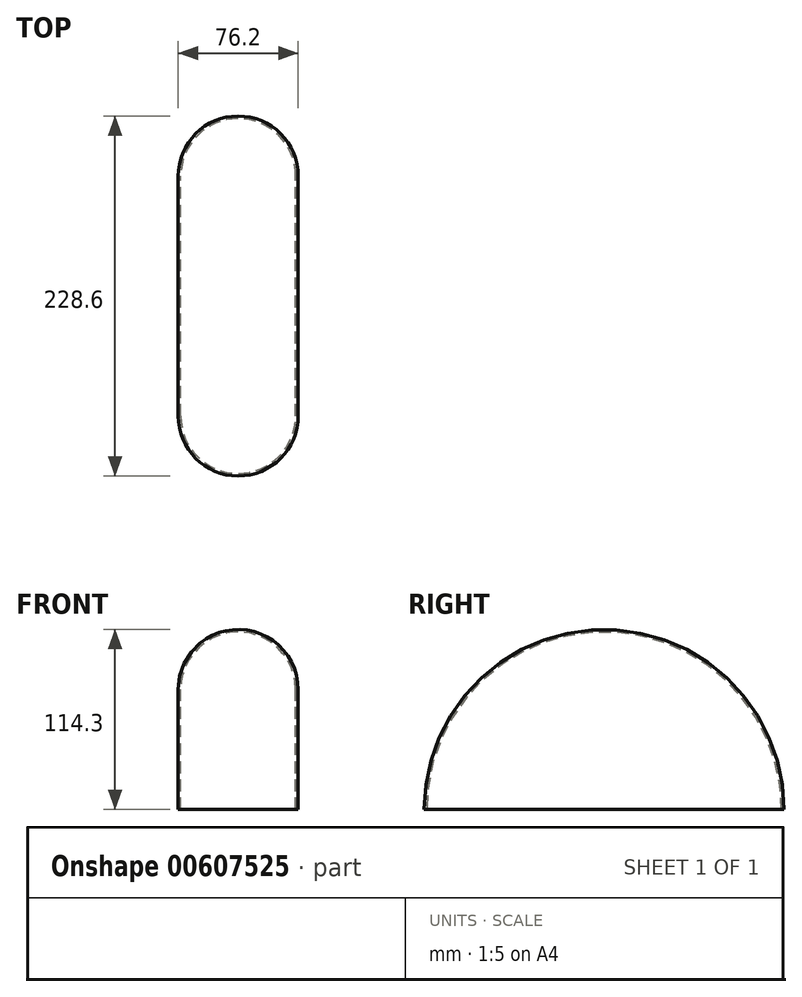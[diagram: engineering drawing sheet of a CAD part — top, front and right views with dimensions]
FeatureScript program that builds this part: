
annotation { "Feature Type Name" : "Feature", "Feature Type Description" : "" }
export const myFeature = defineFeature(function(context is Context, id is Id, definition is map)
    precondition{}
    {
        {
            var Q0;
            Q0=qCreatedBy(makeId("Top.planeOp"),FACE);
            var sketch = newSketch(context, id + "F0", { "sketchPlane" : qUnion([Q0])});
            skLineSegment(sketch, "E0", {"start": v(0, 0) * mm, "end": v(38.1, 0) * mm});
            skLineSegment(sketch, "E1", {"start": v(0, 0) * mm, "end": v(-38.1, 0) * mm});
            skLineSegment(sketch, "E2", {"start": v(-38.1, 0) * mm, "end": v(-38.1, 114.3) * mm});
            skLineSegment(sketch, "E3", {"start": v(-38.1, 114.3) * mm, "end": v(38.1, 114.3) * mm});
            skLineSegment(sketch, "E4", {"start": v(38.1, 114.3) * mm, "end": v(38.1, 0) * mm});
            skLineSegment(sketch, "E5", {"start": v(0, 114.3) * mm, "end": v(0, 76.2) * mm});
            skArc(sketch, "E6", {"start": v(38.1, 76.2) * mm, "mid": v(0, 114.3) * mm, "end": v(-38.1, 76.2) * mm});
            skLineSegment(sketch, "E7", {"start": v(-38.1, 76.2) * mm, "end": v(-36.51, 76.2) * mm});
            skLineSegment(sketch, "E8", {"start": v(38.1, 76.2) * mm, "end": v(36.51, 76.2) * mm});
            skArc(sketch, "E9", {"start": v(36.51, 76.2) * mm, "mid": v(0, 112.71) * mm, "end": v(-36.51, 76.2) * mm});
            skLineSegment(sketch, "E10", {"start": v(-36.51, 76.2) * mm, "end": v(-36.51, 0) * mm});
            skLineSegment(sketch, "E11", {"start": v(36.51, 76.2) * mm, "end": v(36.51, 0) * mm});
            skSolve(sketch);
        }
        {
            var Q0;
            {var subQ5=sQuery(id+"F0.wireOp",EDGE,"E8");Q0=makeQuery(id+"F0.imprint","IMPRINT",FACE,{"disambiguationData":[TD([[makeQuery(id+"F0.imprint","IMPRINT",EDGE,{"derivedFrom":subQ5}),-1.0]])]});}
            var Q1;
            {var subQ5=sQuery(id+"F0.wireOp",EDGE,"E7");Q1=makeQuery(id+"F0.imprint","IMPRINT",FACE,{"disambiguationData":[TD([[makeQuery(id+"F0.imprint","IMPRINT",EDGE,{"derivedFrom":subQ5}),1.0]])]});}
            var Q2;
            {var subQ4=sQuery(id+"F0.wireOp",EDGE,"E8");Q2=makeQuery(id+"F0.imprint","IMPRINT",FACE,{"disambiguationData":[TD([[makeQuery(id+"F0.imprint","IMPRINT",EDGE,{"derivedFrom":subQ4}),1.0]])]});}
            var Q3;
            {var subQ4=sQuery(id+"F0.wireOp",EDGE,"E7");Q3=makeQuery(id+"F0.imprint","IMPRINT",FACE,{"disambiguationData":[TD([[makeQuery(id+"F0.imprint","IMPRINT",EDGE,{"derivedFrom":subQ4}),-1.0]])]});}
            var Q4;
            Q4=sQuery(id+"F0.wireOp",EDGE,"E1");
            revolve(context, id + "F1", {"surfaceOperationType" : NewSurfaceOperationType.NEW, "entities" : qUnion([Q0, Q1, Q2, Q3]), "axis" : qUnion([Q4]), "revolveType" : RevolveType.ONE_DIRECTION, "oppositeDirection" : true, "angle" : 180 * degree});
        }
    });
